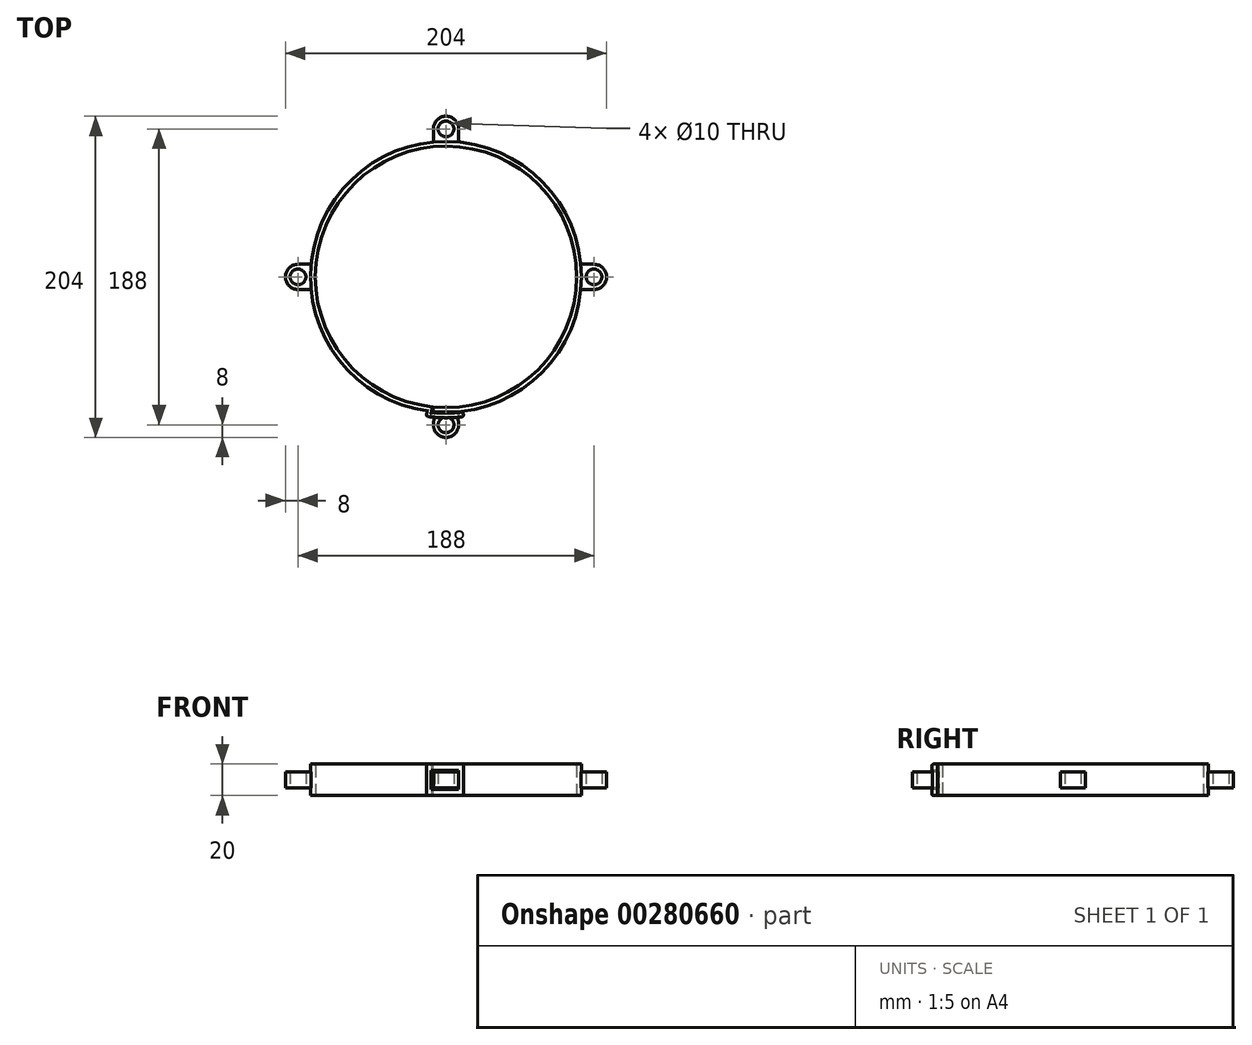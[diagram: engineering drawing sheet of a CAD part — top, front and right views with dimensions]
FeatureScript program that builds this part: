
annotation { "Feature Type Name" : "Feature", "Feature Type Description" : "" }
export const myFeature = defineFeature(function(context is Context, id is Id, definition is map)
    precondition{}
    {
        {
            var Q0;
            Q0=qCreatedBy(makeId("Right.planeOp"),FACE);
            var sketch = newSketch(context, id + "F0", { "sketchPlane" : qUnion([Q0])});
            skLineSegment(sketch, "E0.bottom", {"start": v(83, -10) * mm, "end": v(86, -10) * mm});
            skLineSegment(sketch, "E0.top", {"start": v(83, 10) * mm, "end": v(86, 10) * mm});
            skLineSegment(sketch, "E0.left", {"start": v(83, -10) * mm, "end": v(83, 10) * mm});
            skLineSegment(sketch, "E0.right", {"start": v(86, -10) * mm, "end": v(86, 10) * mm});
            skLineSegment(sketch, "E1", {"start": v(0, 0) * mm, "end": v(0, 60.92) * mm, "construction": true});
            skLineSegment(sketch, "E2", {"start": v(0, 0) * mm, "end": v(83, 0) * mm, "construction": true});
            skSolve(sketch);
        }
        {
            var Q0;
            Q0=makeQuery(id+"F0.imprint","IMPRINT",FACE,{"disambiguationData":[TD([[makeQuery(id+"F0.imprint","IMPRINT",EDGE,{"derivedFrom":sQuery(id+"F0.wireOp",EDGE,"E0.bottom")}),1.0]])]});
            var Q1;
            Q1=sQuery(id+"F0.wireOp",EDGE,"E1");
            revolve(context, id + "F1", {"entities" : qUnion([Q0]), "axis" : qUnion([Q1]), "revolveType" : RevolveType.FULL});
        }
        {
            var Q0;
            Q0=qCreatedBy(makeId("Top.planeOp"),FACE);
            var sketch = newSketch(context, id + "F2", { "sketchPlane" : qUnion([Q0])});
            skLineSegment(sketch, "E3", {"start": v(0, 0) * mm, "end": v(0, 94) * mm, "construction": true});
            skCircle(sketch, "E4", {"center": v(0, 94) * mm, "radius": 8 * mm});
            skCircle(sketch, "E5", {"center": v(0, 94) * mm, "radius": 5 * mm});
            skLineSegment(sketch, "E6", {"start": v(-8, 94) * mm, "end": v(-8, 85.63) * mm});
            skLineSegment(sketch, "E7.MirrorCS", {"start": v(8, 94) * mm, "end": v(8, 85.63) * mm});
            skCircle(sketch, "E8.0", {"center": v(0, 0) * mm, "radius": 86 * mm});
            skCircle(sketch, "E9.0", {"center": v(0, 0) * mm, "radius": 83 * mm});
            skLineSegment(sketch, "E10", {"start": v(0, 0) * mm, "end": v(0, -94) * mm, "construction": true});
            skCircle(sketch, "E11", {"center": v(0, -94) * mm, "radius": 8 * mm});
            skCircle(sketch, "E12", {"center": v(0, -94) * mm, "radius": 5 * mm});
            skLineSegment(sketch, "E13", {"start": v(-7.32, -85.69) * mm, "end": v(-7.97, -93.32) * mm});
            skLineSegment(sketch, "E14.MirrorCS", {"start": v(7.32, -85.69) * mm, "end": v(7.97, -93.32) * mm});
            skCircle(sketch, "E15.0", {"center": v(0, 0) * mm, "radius": 86.5 * mm});
            skCircle(sketch, "E16.0", {"center": v(0, 0) * mm, "radius": 89.5 * mm});
            skLineSegment(sketch, "E17.0", {"start": v(7.86, -86.14) * mm, "end": v(8.12, -89.13) * mm});
            skLineSegment(sketch, "E18.0", {"start": v(10.84, -85.82) * mm, "end": v(11.1, -88.8) * mm});
            skLineSegment(sketch, "E19", {"start": v(-9.14, -86.02) * mm, "end": v(-9.4, -89) * mm});
            skLineSegment(sketch, "E20", {"start": v(-9.14, -86.02) * mm, "end": v(-8.84, -82.53) * mm});
            skLineSegment(sketch, "E21", {"start": v(-8.6, -85.57) * mm, "end": v(-8.34, -82.58) * mm});
            skLineSegment(sketch, "E22", {"start": v(-11.82, -82.15) * mm, "end": v(-12.38, -88.64) * mm});
            skCircle(sketch, "E23.1.0", {"center": v(94, 0) * mm, "radius": 5 * mm});
            skCircle(sketch, "E23.1.1", {"center": v(94, 0) * mm, "radius": 8 * mm});
            skLineSegment(sketch, "E23.1.2", {"start": v(94, 8) * mm, "end": v(85.63, 8) * mm});
            skLineSegment(sketch, "E23.1.3", {"start": v(94, -8) * mm, "end": v(85.63, -8) * mm});
            skLineSegment(sketch, "E23.anchor1", {"start": v(0, 0) * mm, "end": v(-8, 85.63) * mm, "construction": true});
            skLineSegment(sketch, "E23.anchor2", {"start": v(0, 0) * mm, "end": v(85.63, 8) * mm, "construction": true});
            skCircle(sketch, "E24.1.0", {"center": v(-94, 0) * mm, "radius": 8 * mm});
            skLineSegment(sketch, "E24.1.1", {"start": v(-94, -8) * mm, "end": v(-85.63, -8) * mm});
            skLineSegment(sketch, "E24.1.2", {"start": v(-94, 8) * mm, "end": v(-85.63, 8) * mm});
            skCircle(sketch, "E24.1.3", {"center": v(-94, 0) * mm, "radius": 5 * mm});
            skLineSegment(sketch, "E24.anchor2", {"start": v(0, 0) * mm, "end": v(-85.63, -8) * mm, "construction": true});
            skSolve(sketch);
        }
        {
            var Q0;
            {var subQ0=sQuery(id+"F2.wireOp",EDGE,"E8.0");var subQ1=sQuery(id+"F2.wireOp",EDGE,"E4");var subQ2=makeQuery(id+"F2.imprint","INTERSECT",VERTEX,{"derivedFrom":[subQ1,subQ0]});Q0=makeQuery(id+"F2.imprint","IMPRINT",FACE,{"disambiguationData":[TD([[makeQuery(id+"F2.imprint","IMPRINT",EDGE,{"disambiguationData":[TD([[subQ2,-1.0]])],"derivedFrom":subQ1}),-1.0]])]});}
            var Q1;
            {var subQ0=sQuery(id+"F2.wireOp",EDGE,"E15.0");var subQ1=sQuery(id+"F2.wireOp",EDGE,"E4");var subQ2=makeQuery(id+"F2.imprint","INTERSECT",VERTEX,{"disambiguationData":[OD(0.0)],"derivedFrom":[subQ1,subQ0]});Q1=makeQuery(id+"F2.imprint","IMPRINT",FACE,{"disambiguationData":[TD([[makeQuery(id+"F2.imprint","IMPRINT",EDGE,{"disambiguationData":[TD([[subQ2,-1.0]])],"derivedFrom":subQ1}),1.0]])]});}
            var Q2;
            {var subQ0=sQuery(id+"F2.wireOp",EDGE,"E15.0");var subQ1=sQuery(id+"F2.wireOp",EDGE,"E4");var subQ2=makeQuery(id+"F2.imprint","INTERSECT",VERTEX,{"disambiguationData":[OD(0.0)],"derivedFrom":[subQ1,subQ0]});Q2=makeQuery(id+"F2.imprint","IMPRINT",FACE,{"disambiguationData":[TD([[makeQuery(id+"F2.imprint","IMPRINT",EDGE,{"disambiguationData":[TD([[subQ2,-1.0]])],"derivedFrom":subQ1}),-1.0]])]});}
            var Q3;
            {var subQ0=sQuery(id+"F2.wireOp",EDGE,"E16.0");var subQ1=sQuery(id+"F2.wireOp",EDGE,"E4");var subQ2=makeQuery(id+"F2.imprint","INTERSECT",VERTEX,{"disambiguationData":[OD(0.0)],"derivedFrom":[subQ1,subQ0]});Q3=makeQuery(id+"F2.imprint","IMPRINT",FACE,{"disambiguationData":[TD([[makeQuery(id+"F2.imprint","IMPRINT",EDGE,{"disambiguationData":[TD([[subQ2,-1.0]])],"derivedFrom":subQ1}),-1.0]])]});}
            var Q4;
            {var subQ0=sQuery(id+"F2.wireOp",EDGE,"E15.0");var subQ1=sQuery(id+"F2.wireOp",EDGE,"E4");var subQ2=makeQuery(id+"F2.imprint","INTERSECT",VERTEX,{"disambiguationData":[OD(1.0)],"derivedFrom":[subQ1,subQ0]});Q4=makeQuery(id+"F2.imprint","IMPRINT",FACE,{"disambiguationData":[TD([[makeQuery(id+"F2.imprint","IMPRINT",EDGE,{"disambiguationData":[TD([[subQ2,-1.0]])],"derivedFrom":subQ1}),-1.0]])]});}
            var Q5;
            {var subQ0=sQuery(id+"F2.wireOp",EDGE,"E7.MirrorCS");var subQ1=sQuery(id+"F2.wireOp",EDGE,"E4");var subQ2=makeQuery(id+"F2.imprint","INTERSECT",VERTEX,{"derivedFrom":[subQ1,subQ0]});Q5=makeQuery(id+"F2.imprint","IMPRINT",FACE,{"disambiguationData":[TD([[makeQuery(id+"F2.imprint","IMPRINT",EDGE,{"disambiguationData":[TD([[subQ2,1.0]])],"derivedFrom":subQ1}),-1.0]])]});}
            var Q6;
            {var subQ0=sQuery(id+"F2.wireOp",EDGE,"E6");var subQ1=sQuery(id+"F2.wireOp",EDGE,"E4");var subQ2=makeQuery(id+"F2.imprint","INTERSECT",VERTEX,{"derivedFrom":[subQ1,subQ0]});Q6=makeQuery(id+"F2.imprint","IMPRINT",FACE,{"disambiguationData":[TD([[makeQuery(id+"F2.imprint","IMPRINT",EDGE,{"disambiguationData":[TD([[subQ2,-1.0]])],"derivedFrom":subQ1}),-1.0]])]});}
            var Q7;
            {var subQ4=sQuery(id+"F2.wireOp",EDGE,"E4");var subQ7=makeQuery(id+"F2.imprint","INTERSECT",VERTEX,{"derivedFrom":[subQ4,sQuery(id+"F2.wireOp",EDGE,"E6")]});Q7=makeQuery(id+"F2.imprint","IMPRINT",FACE,{"disambiguationData":[TD([[makeQuery(id+"F2.imprint","IMPRINT",EDGE,{"disambiguationData":[TD([[subQ7,1.0]])],"derivedFrom":subQ4}),1.0]])]});}
            var Q8;
            {var subQ1=sQuery(id+"F2.wireOp",EDGE,"E4");var subQ4=sQuery(id+"F2.wireOp",EDGE,"E16.0");var subQ9=makeQuery(id+"F2.imprint","INTERSECT",VERTEX,{"disambiguationData":[OD(0.0)],"derivedFrom":[subQ1,subQ4]});Q8=makeQuery(id+"F2.imprint","IMPRINT",FACE,{"disambiguationData":[TD([[makeQuery(id+"F2.imprint","IMPRINT",EDGE,{"disambiguationData":[TD([[subQ9,-1.0]])],"derivedFrom":subQ1}),1.0]])]});}
            extrude(context, id + "F3", {"entities" : qUnion([Q0, Q1, Q2, Q3, Q4, Q5, Q6, Q7, Q8]), "operationType" : NewBodyOperationType.ADD, "endBound" : BoundingType.SYMMETRIC, "depth" : 10 * mm});
        }
        {
            var Q0;
            {var subQ0=sQuery(id+"F2.wireOp",EDGE,"E21");Q0=makeQuery(id+"F2.imprint","IMPRINT",FACE,{"disambiguationData":[TD([[makeQuery(id+"F2.imprint","IMPRINT",EDGE,{"derivedFrom":subQ0}),1.0]])]});}
            extrude(context, id + "F4", {"entities" : qUnion([Q0]), "operationType" : NewBodyOperationType.REMOVE, "endBound" : BoundingType.THROUGH_ALL, "oppositeDirection" : true, "depth" : 20 * mm});
        }
        {
            var Q0;
            {var subQ0=sQuery(id+"F2.wireOp",EDGE,"E21");Q0=makeQuery(id+"F2.imprint","IMPRINT",FACE,{"disambiguationData":[TD([[makeQuery(id+"F2.imprint","IMPRINT",EDGE,{"derivedFrom":subQ0}),1.0]])]});}
            extrude(context, id + "F5", {"entities" : qUnion([Q0]), "operationType" : NewBodyOperationType.REMOVE, "endBound" : BoundingType.THROUGH_ALL, "depth" : 25 * mm});
        }
        {
            var Q0;
            {var subQ0=sQuery(id+"F2.wireOp",EDGE,"E22");var subQ1=sQuery(id+"F2.wireOp",EDGE,"E8.0");var subQ2=makeQuery(id+"F2.imprint","INTERSECT",VERTEX,{"derivedFrom":[subQ1,subQ0]});Q0=makeQuery(id+"F2.imprint","IMPRINT",FACE,{"disambiguationData":[TD([[makeQuery(id+"F2.imprint","IMPRINT",EDGE,{"disambiguationData":[TD([[subQ2,-1.0]])],"derivedFrom":subQ1}),-1.0]])]});}
            var Q1;
            {var subQ0=sQuery(id+"F2.wireOp",EDGE,"E19");Q1=makeQuery(id+"F2.imprint","IMPRINT",FACE,{"disambiguationData":[TD([[makeQuery(id+"F2.imprint","IMPRINT",EDGE,{"derivedFrom":subQ0}),-1.0]])]});}
            var Q2;
            {var subQ5=sQuery(id+"F2.wireOp",EDGE,"E19");Q2=makeQuery(id+"F2.imprint","IMPRINT",FACE,{"disambiguationData":[TD([[makeQuery(id+"F2.imprint","IMPRINT",EDGE,{"derivedFrom":subQ5}),1.0]])]});}
            var Q3;
            {var subQ0=sQuery(id+"F2.wireOp",EDGE,"E15.0");var subQ1=sQuery(id+"F2.wireOp",EDGE,"E11");var subQ2=makeQuery(id+"F2.imprint","INTERSECT",VERTEX,{"disambiguationData":[OD(1.0)],"derivedFrom":[subQ1,subQ0]});Q3=makeQuery(id+"F2.imprint","IMPRINT",FACE,{"disambiguationData":[TD([[makeQuery(id+"F2.imprint","IMPRINT",EDGE,{"disambiguationData":[TD([[subQ2,-1.0]])],"derivedFrom":subQ1}),-1.0]])]});}
            var Q4;
            {var subQ1=sQuery(id+"F2.wireOp",EDGE,"E11");var subQ4=sQuery(id+"F2.wireOp",EDGE,"E16.0");var subQ9=makeQuery(id+"F2.imprint","INTERSECT",VERTEX,{"disambiguationData":[OD(0.0)],"derivedFrom":[subQ1,subQ4]});Q4=makeQuery(id+"F2.imprint","IMPRINT",FACE,{"disambiguationData":[TD([[makeQuery(id+"F2.imprint","IMPRINT",EDGE,{"disambiguationData":[TD([[subQ9,-1.0]])],"derivedFrom":subQ1}),1.0]])]});}
            var Q5;
            {var subQ0=sQuery(id+"F2.wireOp",EDGE,"E16.0");var subQ1=sQuery(id+"F2.wireOp",EDGE,"E12");var subQ2=makeQuery(id+"F2.imprint","INTERSECT",VERTEX,{"disambiguationData":[OD(0.0)],"derivedFrom":[subQ1,subQ0]});Q5=makeQuery(id+"F2.imprint","IMPRINT",FACE,{"disambiguationData":[TD([[makeQuery(id+"F2.imprint","IMPRINT",EDGE,{"disambiguationData":[TD([[subQ2,1.0]])],"derivedFrom":subQ1}),1.0]])]});}
            var Q6;
            {var subQ0=sQuery(id+"F2.wireOp",EDGE,"E16.0");var subQ1=sQuery(id+"F2.wireOp",EDGE,"E11");var subQ2=makeQuery(id+"F2.imprint","INTERSECT",VERTEX,{"disambiguationData":[OD(0.0)],"derivedFrom":[subQ1,subQ0]});Q6=makeQuery(id+"F2.imprint","IMPRINT",FACE,{"disambiguationData":[TD([[makeQuery(id+"F2.imprint","IMPRINT",EDGE,{"disambiguationData":[TD([[subQ2,-1.0]])],"derivedFrom":subQ1}),-1.0]])]});}
            var Q7;
            {var subQ5=sQuery(id+"F2.wireOp",EDGE,"E17.0");Q7=makeQuery(id+"F2.imprint","IMPRINT",FACE,{"disambiguationData":[TD([[makeQuery(id+"F2.imprint","IMPRINT",EDGE,{"derivedFrom":subQ5}),-1.0]])]});}
            var Q8;
            {var subQ0=sQuery(id+"F2.wireOp",EDGE,"E17.0");Q8=makeQuery(id+"F2.imprint","IMPRINT",FACE,{"disambiguationData":[TD([[makeQuery(id+"F2.imprint","IMPRINT",EDGE,{"derivedFrom":subQ0}),1.0]])]});}
            extrude(context, id + "F6", {"entities" : qUnion([Q0, Q1, Q2, Q3, Q4, Q5, Q6, Q7, Q8]), "operationType" : NewBodyOperationType.ADD, "endBound" : BoundingType.SYMMETRIC, "depth" : 20 * mm});
        }
        {
            var Q0;
            {var subQ5=sQuery(id+"F2.wireOp",EDGE,"E19");Q0=makeQuery(id+"F2.imprint","IMPRINT",FACE,{"disambiguationData":[TD([[makeQuery(id+"F2.imprint","IMPRINT",EDGE,{"derivedFrom":subQ5}),1.0]])]});}
            var Q1;
            {var subQ0=sQuery(id+"F2.wireOp",EDGE,"E15.0");var subQ1=sQuery(id+"F2.wireOp",EDGE,"E11");var subQ2=makeQuery(id+"F2.imprint","INTERSECT",VERTEX,{"disambiguationData":[OD(1.0)],"derivedFrom":[subQ1,subQ0]});Q1=makeQuery(id+"F2.imprint","IMPRINT",FACE,{"disambiguationData":[TD([[makeQuery(id+"F2.imprint","IMPRINT",EDGE,{"disambiguationData":[TD([[subQ2,-1.0]])],"derivedFrom":subQ1}),-1.0]])]});}
            var Q2;
            {var subQ1=sQuery(id+"F2.wireOp",EDGE,"E11");var subQ4=sQuery(id+"F2.wireOp",EDGE,"E16.0");var subQ9=makeQuery(id+"F2.imprint","INTERSECT",VERTEX,{"disambiguationData":[OD(0.0)],"derivedFrom":[subQ1,subQ4]});Q2=makeQuery(id+"F2.imprint","IMPRINT",FACE,{"disambiguationData":[TD([[makeQuery(id+"F2.imprint","IMPRINT",EDGE,{"disambiguationData":[TD([[subQ9,-1.0]])],"derivedFrom":subQ1}),1.0]])]});}
            var Q3;
            {var subQ0=sQuery(id+"F2.wireOp",EDGE,"E16.0");var subQ1=sQuery(id+"F2.wireOp",EDGE,"E12");var subQ2=makeQuery(id+"F2.imprint","INTERSECT",VERTEX,{"disambiguationData":[OD(0.0)],"derivedFrom":[subQ1,subQ0]});Q3=makeQuery(id+"F2.imprint","IMPRINT",FACE,{"disambiguationData":[TD([[makeQuery(id+"F2.imprint","IMPRINT",EDGE,{"disambiguationData":[TD([[subQ2,1.0]])],"derivedFrom":subQ1}),1.0]])]});}
            var Q4;
            {var subQ0=sQuery(id+"F2.wireOp",EDGE,"E16.0");var subQ1=sQuery(id+"F2.wireOp",EDGE,"E11");var subQ2=makeQuery(id+"F2.imprint","INTERSECT",VERTEX,{"disambiguationData":[OD(0.0)],"derivedFrom":[subQ1,subQ0]});Q4=makeQuery(id+"F2.imprint","IMPRINT",FACE,{"disambiguationData":[TD([[makeQuery(id+"F2.imprint","IMPRINT",EDGE,{"disambiguationData":[TD([[subQ2,-1.0]])],"derivedFrom":subQ1}),-1.0]])]});}
            var Q5;
            {var subQ5=sQuery(id+"F2.wireOp",EDGE,"E17.0");Q5=makeQuery(id+"F2.imprint","IMPRINT",FACE,{"disambiguationData":[TD([[makeQuery(id+"F2.imprint","IMPRINT",EDGE,{"derivedFrom":subQ5}),-1.0]])]});}
            extrude(context, id + "F7", {"entities" : qUnion([Q0, Q1, Q2, Q3, Q4, Q5]), "operationType" : NewBodyOperationType.REMOVE, "endBound" : BoundingType.SYMMETRIC, "oppositeDirection" : true, "depth" : 12 * mm});
        }
        {
            var Q0;
            {var subQ0=sQuery(id+"F2.wireOp",EDGE,"E13");var subQ1=sQuery(id+"F2.wireOp",EDGE,"E8.0");var subQ2=makeQuery(id+"F2.imprint","INTERSECT",VERTEX,{"derivedFrom":[subQ1,subQ0]});Q0=makeQuery(id+"F2.imprint","IMPRINT",FACE,{"disambiguationData":[TD([[makeQuery(id+"F2.imprint","IMPRINT",EDGE,{"disambiguationData":[TD([[subQ2,-1.0]])],"derivedFrom":subQ1}),-1.0]])]});}
            var Q1;
            {var subQ0=sQuery(id+"F2.wireOp",EDGE,"E11");var subQ1=makeQuery(id+"F2.imprint","INTERSECT",VERTEX,{"derivedFrom":[sQuery(id+"F2.wireOp",EDGE,"E8.0"),subQ0]});Q1=makeQuery(id+"F2.imprint","IMPRINT",FACE,{"disambiguationData":[TD([[makeQuery(id+"F2.imprint","IMPRINT",EDGE,{"disambiguationData":[TD([[subQ1,1.0]])],"derivedFrom":subQ0}),1.0]])]});}
            var Q2;
            {var subQ0=sQuery(id+"F2.wireOp",EDGE,"E14.MirrorCS");var subQ1=sQuery(id+"F2.wireOp",EDGE,"E8.0");var subQ2=makeQuery(id+"F2.imprint","INTERSECT",VERTEX,{"derivedFrom":[subQ1,subQ0]});Q2=makeQuery(id+"F2.imprint","IMPRINT",FACE,{"disambiguationData":[TD([[makeQuery(id+"F2.imprint","IMPRINT",EDGE,{"disambiguationData":[TD([[subQ2,1.0]])],"derivedFrom":subQ1}),-1.0]])]});}
            var Q3;
            {var subQ0=sQuery(id+"F2.wireOp",EDGE,"E16.0");var subQ1=sQuery(id+"F2.wireOp",EDGE,"E11");var subQ2=makeQuery(id+"F2.imprint","INTERSECT",VERTEX,{"disambiguationData":[OD(0.0)],"derivedFrom":[subQ1,subQ0]});Q3=makeQuery(id+"F2.imprint","IMPRINT",FACE,{"disambiguationData":[TD([[makeQuery(id+"F2.imprint","IMPRINT",EDGE,{"disambiguationData":[TD([[subQ2,-1.0]])],"derivedFrom":subQ1}),-1.0]])]});}
            var Q4;
            {var subQ1=sQuery(id+"F2.wireOp",EDGE,"E11");var subQ4=sQuery(id+"F2.wireOp",EDGE,"E16.0");var subQ9=makeQuery(id+"F2.imprint","INTERSECT",VERTEX,{"disambiguationData":[OD(0.0)],"derivedFrom":[subQ1,subQ4]});Q4=makeQuery(id+"F2.imprint","IMPRINT",FACE,{"disambiguationData":[TD([[makeQuery(id+"F2.imprint","IMPRINT",EDGE,{"disambiguationData":[TD([[subQ9,-1.0]])],"derivedFrom":subQ1}),1.0]])]});}
            var Q5;
            {var subQ0=sQuery(id+"F2.wireOp",EDGE,"E15.0");var subQ1=sQuery(id+"F2.wireOp",EDGE,"E11");var subQ2=makeQuery(id+"F2.imprint","INTERSECT",VERTEX,{"disambiguationData":[OD(1.0)],"derivedFrom":[subQ1,subQ0]});Q5=makeQuery(id+"F2.imprint","IMPRINT",FACE,{"disambiguationData":[TD([[makeQuery(id+"F2.imprint","IMPRINT",EDGE,{"disambiguationData":[TD([[subQ2,-1.0]])],"derivedFrom":subQ1}),-1.0]])]});}
            var Q6;
            {var subQ0=sQuery(id+"F2.wireOp",EDGE,"E13");var subQ1=sQuery(id+"F2.wireOp",EDGE,"E11");var subQ2=makeQuery(id+"F2.imprint","INTERSECT",VERTEX,{"derivedFrom":[subQ1,subQ0]});Q6=makeQuery(id+"F2.imprint","IMPRINT",FACE,{"disambiguationData":[TD([[makeQuery(id+"F2.imprint","IMPRINT",EDGE,{"disambiguationData":[TD([[subQ2,1.0]])],"derivedFrom":subQ1}),-1.0]])]});}
            var Q7;
            {var subQ0=sQuery(id+"F2.wireOp",EDGE,"E14.MirrorCS");var subQ1=sQuery(id+"F2.wireOp",EDGE,"E11");var subQ2=makeQuery(id+"F2.imprint","INTERSECT",VERTEX,{"derivedFrom":[subQ1,subQ0]});Q7=makeQuery(id+"F2.imprint","IMPRINT",FACE,{"disambiguationData":[TD([[makeQuery(id+"F2.imprint","IMPRINT",EDGE,{"disambiguationData":[TD([[subQ2,-1.0]])],"derivedFrom":subQ1}),-1.0]])]});}
            var Q8;
            {var subQ4=sQuery(id+"F2.wireOp",EDGE,"E11");var subQ6=makeQuery(id+"F2.imprint","INTERSECT",VERTEX,{"derivedFrom":[subQ4,sQuery(id+"F2.wireOp",EDGE,"E14.MirrorCS")]});Q8=makeQuery(id+"F2.imprint","IMPRINT",FACE,{"disambiguationData":[TD([[makeQuery(id+"F2.imprint","IMPRINT",EDGE,{"disambiguationData":[TD([[subQ6,-1.0]])],"derivedFrom":subQ4}),1.0]])]});}
            extrude(context, id + "F8", {"entities" : qUnion([Q0, Q1, Q2, Q3, Q4, Q5, Q6, Q7, Q8]), "operationType" : NewBodyOperationType.ADD, "endBound" : BoundingType.SYMMETRIC, "depth" : 10 * mm});
        }
        {
            var Q0;
            Q0=makeQuery(id+"F6.opExtrude","CAP_EDGE",EDGE,{"disambiguationData":[OSD([sQuery(id+"F2.wireOp",EDGE,"E16.0")])],"isStart":false});
            var Q1;
            Q1=makeQuery(id+"F6.opExtrude","SWEPT_EDGE",EDGE,{"disambiguationData":[OSD([sQuery(id+"F2.wireOp",EDGE,"E16.0"),sQuery(id+"F2.wireOp",EDGE,"E18.0")])]});
            var Q2;
            Q2=makeQuery(id+"F6.opExtrude","CAP_EDGE",EDGE,{"disambiguationData":[OSD([sQuery(id+"F2.wireOp",EDGE,"E18.0")])],"isStart":false});
            var Q3;
            Q3=makeQuery(id+"F6.opExtrude","CAP_EDGE",EDGE,{"disambiguationData":[OSD([sQuery(id+"F2.wireOp",EDGE,"E18.0")])],"isStart":true});
            var Q4;
            Q4=makeQuery(id+"F6.opExtrude","CAP_EDGE",EDGE,{"disambiguationData":[OSD([sQuery(id+"F2.wireOp",EDGE,"E16.0")])],"isStart":true});
            var Q5;
            Q5=makeQuery(id+"F6.opExtrude","SWEPT_EDGE",EDGE,{"disambiguationData":[OSD([sQuery(id+"F2.wireOp",EDGE,"E16.0"),sQuery(id+"F2.wireOp",EDGE,"E22")])]});
            var Q6;
            Q6=makeQuery(id+"F6.opExtrude","SWEPT_EDGE",EDGE,{"disambiguationData":[OSD([sQuery(id+"F2.wireOp",EDGE,"E8.0"),sQuery(id+"F2.wireOp",EDGE,"E22")])]});
            var Q7;
            Q7=makeQuery(id+"F6.opExtrude","CAP_EDGE",EDGE,{"disambiguationData":[OSD([sQuery(id+"F2.wireOp",EDGE,"E22")])],"isStart":false});
            var Q8;
            Q8=makeQuery(id+"F6.opExtrude","CAP_EDGE",EDGE,{"disambiguationData":[OSD([sQuery(id+"F2.wireOp",EDGE,"E22")])],"isStart":true});
            var Q9;
            {var subQ0=sQuery(id+"F2.wireOp",EDGE,"E20");Q9=makeQuery(id+"F6.boolean.opBoolean","MERGE",EDGE,{"derivedFrom":[makeQuery(id+"F5.boolean.opBoolean","INTERSECT",EDGE,{"derivedFrom":[makeQuery(id+"F1.opRevolve","SWEPT_FACE",FACE,{"disambiguationData":[OSD([sQuery(id+"F0.wireOp",EDGE,"E0.top")])]}),makeQuery(id+"F5.opExtrude","SWEPT_FACE",FACE,{"disambiguationData":[OSD([subQ0])]})]}),makeQuery(id+"F6.opExtrude","CAP_EDGE",EDGE,{"disambiguationData":[OSD([subQ0])],"isStart":false})]});}
            var Q10;
            Q10=makeQuery(id+"F5.boolean.opBoolean","INTERSECT",EDGE,{"derivedFrom":[makeQuery(id+"F1.opRevolve","SWEPT_FACE",FACE,{"disambiguationData":[OSD([sQuery(id+"F0.wireOp",EDGE,"E0.top")])]}),makeQuery(id+"F5.opExtrude","SWEPT_FACE",FACE,{"disambiguationData":[OSD([sQuery(id+"F2.wireOp",EDGE,"E21")])]})]});
            var Q11;
            Q11=makeQuery(id+"F1.opRevolve","SWEPT_EDGE",EDGE,{"disambiguationData":[OSD([sQuery(id+"F0.wireOp",EDGE,"E0.top"),sQuery(id+"F0.wireOp",EDGE,"E0.left")])]});
            var Q12;
            Q12=makeQuery(id+"F1.opRevolve","SWEPT_EDGE",EDGE,{"disambiguationData":[OSD([sQuery(id+"F0.wireOp",EDGE,"E0.bottom"),sQuery(id+"F0.wireOp",EDGE,"E0.left")])]});
            var Q13;
            Q13=makeQuery(id+"F4.boolean.opBoolean","INTERSECT",EDGE,{"derivedFrom":[makeQuery(id+"F1.opRevolve","SWEPT_FACE",FACE,{"disambiguationData":[OSD([sQuery(id+"F0.wireOp",EDGE,"E0.bottom")])]}),makeQuery(id+"F4.opExtrude","SWEPT_FACE",FACE,{"disambiguationData":[OSD([sQuery(id+"F2.wireOp",EDGE,"E21")])]})]});
            var Q14;
            {var subQ0=sQuery(id+"F2.wireOp",EDGE,"E20");Q14=makeQuery(id+"F6.boolean.opBoolean","MERGE",EDGE,{"derivedFrom":[makeQuery(id+"F4.boolean.opBoolean","INTERSECT",EDGE,{"derivedFrom":[makeQuery(id+"F1.opRevolve","SWEPT_FACE",FACE,{"disambiguationData":[OSD([sQuery(id+"F0.wireOp",EDGE,"E0.bottom")])]}),makeQuery(id+"F4.opExtrude","SWEPT_FACE",FACE,{"disambiguationData":[OSD([subQ0])]})]}),makeQuery(id+"F6.opExtrude","CAP_EDGE",EDGE,{"disambiguationData":[OSD([subQ0])],"isStart":true})]});}
            var Q15;
            {var subQ0=sQuery(id+"F2.wireOp",EDGE,"E21");var subQ1=sQuery(id+"F2.wireOp",EDGE,"E9.0");Q15=makeQuery(id+"F5.boolean.opBoolean","MERGE",EDGE,{"derivedFrom":[makeQuery(id+"F4.boolean.opBoolean","COPY",EDGE,{"derivedFrom":makeQuery(id+"F4.opExtrude","SWEPT_EDGE",EDGE,{"disambiguationData":[OSD([subQ1,subQ0])]})}),makeQuery(id+"F5.opExtrude","SWEPT_EDGE",EDGE,{"disambiguationData":[OSD([subQ1,subQ0])]})]});}
            var Q16;
            {var subQ0=sQuery(id+"F2.wireOp",EDGE,"E20");var subQ1=sQuery(id+"F2.wireOp",EDGE,"E9.0");Q16=makeQuery(id+"F5.boolean.opBoolean","MERGE",EDGE,{"derivedFrom":[makeQuery(id+"F4.boolean.opBoolean","COPY",EDGE,{"derivedFrom":makeQuery(id+"F4.opExtrude","SWEPT_EDGE",EDGE,{"disambiguationData":[OSD([subQ1,subQ0])]})}),makeQuery(id+"F5.opExtrude","SWEPT_EDGE",EDGE,{"disambiguationData":[OSD([subQ1,subQ0])]})]});}
            var Q17;
            Q17=makeQuery(id+"F3.opExtrude","CAP_EDGE",EDGE,{"disambiguationData":[OSD([sQuery(id+"F2.wireOp",EDGE,"E8.0")])],"isStart":false});
            var Q18;
            Q18=makeQuery(id+"F3.opExtrude","SWEPT_EDGE",EDGE,{"disambiguationData":[OSD([sQuery(id+"F2.wireOp",EDGE,"E7.MirrorCS"),sQuery(id+"F2.wireOp",EDGE,"E8.0")])]});
            var Q19;
            Q19=makeQuery(id+"F3.opExtrude","SWEPT_EDGE",EDGE,{"disambiguationData":[OSD([sQuery(id+"F2.wireOp",EDGE,"E6"),sQuery(id+"F2.wireOp",EDGE,"E8.0")])]});
            var Q20;
            Q20=makeQuery(id+"F3.opExtrude","CAP_EDGE",EDGE,{"disambiguationData":[OSD([sQuery(id+"F2.wireOp",EDGE,"E8.0")])],"isStart":true});
            var Q21;
            Q21=makeQuery(id+"F6.opExtrude","CAP_EDGE",EDGE,{"disambiguationData":[OSD([sQuery(id+"F2.wireOp",EDGE,"E15.0")])],"isStart":false});
            var Q22;
            Q22=makeQuery(id+"F6.opExtrude","CAP_EDGE",EDGE,{"disambiguationData":[OSD([sQuery(id+"F2.wireOp",EDGE,"E15.0")])],"isStart":true});
            var Q23;
            Q23=makeQuery(id+"F6.opExtrude","SWEPT_EDGE",EDGE,{"disambiguationData":[OSD([sQuery(id+"F2.wireOp",EDGE,"E15.0"),sQuery(id+"F2.wireOp",EDGE,"E18.0")])]});
            fillet(context, id + "F9", {"entities" : qUnion([Q0, Q1, Q2, Q3, Q4, Q5, Q6, Q7, Q8, Q9, Q10, Q11, Q12, Q13, Q14, Q15, Q16, Q17, Q18, Q19, Q20, Q21, Q22, Q23]), "radius" : 1 * mm, "tangentPropagation" : true, "allowEdgeOverflow" : false});
        }
        {
            var Q0;
            {var subQ0=sQuery(id+"F2.wireOp",EDGE,"E24.1.2");var subQ1=sQuery(id+"F2.wireOp",EDGE,"E8.0");var subQ2=makeQuery(id+"F2.imprint","INTERSECT",VERTEX,{"derivedFrom":[subQ1,subQ0]});Q0=makeQuery(id+"F2.imprint","IMPRINT",FACE,{"disambiguationData":[TD([[makeQuery(id+"F2.imprint","IMPRINT",EDGE,{"disambiguationData":[TD([[subQ2,-1.0]])],"derivedFrom":subQ1}),-1.0]])]});}
            var Q1;
            {var subQ0=sQuery(id+"F2.wireOp",EDGE,"E24.1.0");var subQ1=sQuery(id+"F2.wireOp",EDGE,"E15.0");var subQ2=makeQuery(id+"F2.imprint","INTERSECT",VERTEX,{"disambiguationData":[OD(0.0)],"derivedFrom":[subQ1,subQ0]});Q1=makeQuery(id+"F2.imprint","IMPRINT",FACE,{"disambiguationData":[TD([[makeQuery(id+"F2.imprint","IMPRINT",EDGE,{"disambiguationData":[TD([[subQ2,-1.0]])],"derivedFrom":subQ1}),1.0]])]});}
            var Q2;
            {var subQ0=sQuery(id+"F2.wireOp",EDGE,"E24.1.1");var subQ1=sQuery(id+"F2.wireOp",EDGE,"E8.0");var subQ2=makeQuery(id+"F2.imprint","INTERSECT",VERTEX,{"derivedFrom":[subQ1,subQ0]});Q2=makeQuery(id+"F2.imprint","IMPRINT",FACE,{"disambiguationData":[TD([[makeQuery(id+"F2.imprint","IMPRINT",EDGE,{"disambiguationData":[TD([[subQ2,1.0]])],"derivedFrom":subQ1}),-1.0]])]});}
            var Q3;
            {var subQ0=sQuery(id+"F2.wireOp",EDGE,"E24.1.0");var subQ1=sQuery(id+"F2.wireOp",EDGE,"E15.0");var subQ2=makeQuery(id+"F2.imprint","INTERSECT",VERTEX,{"disambiguationData":[OD(1.0)],"derivedFrom":[subQ1,subQ0]});Q3=makeQuery(id+"F2.imprint","IMPRINT",FACE,{"disambiguationData":[TD([[makeQuery(id+"F2.imprint","IMPRINT",EDGE,{"disambiguationData":[TD([[subQ2,-1.0]])],"derivedFrom":subQ1}),-1.0]])]});}
            var Q4;
            {var subQ0=sQuery(id+"F2.wireOp",EDGE,"E24.1.0");var subQ1=sQuery(id+"F2.wireOp",EDGE,"E15.0");var subQ9=makeQuery(id+"F2.imprint","INTERSECT",VERTEX,{"disambiguationData":[OD(0.0)],"derivedFrom":[subQ1,subQ0]});Q4=makeQuery(id+"F2.imprint","IMPRINT",FACE,{"disambiguationData":[TD([[makeQuery(id+"F2.imprint","IMPRINT",EDGE,{"disambiguationData":[TD([[subQ9,-1.0]])],"derivedFrom":subQ1}),-1.0]])]});}
            var Q5;
            {var subQ0=sQuery(id+"F2.wireOp",EDGE,"E24.1.2");var subQ1=sQuery(id+"F2.wireOp",EDGE,"E15.0");var subQ2=makeQuery(id+"F2.imprint","INTERSECT",VERTEX,{"derivedFrom":[subQ1,subQ0]});Q5=makeQuery(id+"F2.imprint","IMPRINT",FACE,{"disambiguationData":[TD([[makeQuery(id+"F2.imprint","IMPRINT",EDGE,{"disambiguationData":[TD([[subQ2,-1.0]])],"derivedFrom":subQ1}),-1.0]])]});}
            var Q6;
            {var subQ0=sQuery(id+"F2.wireOp",EDGE,"E24.1.2");var subQ1=sQuery(id+"F2.wireOp",EDGE,"E16.0");var subQ2=makeQuery(id+"F2.imprint","INTERSECT",VERTEX,{"derivedFrom":[subQ1,subQ0]});Q6=makeQuery(id+"F2.imprint","IMPRINT",FACE,{"disambiguationData":[TD([[makeQuery(id+"F2.imprint","IMPRINT",EDGE,{"disambiguationData":[TD([[subQ2,-1.0]])],"derivedFrom":subQ1}),-1.0]])]});}
            var Q7;
            {var subQ0=sQuery(id+"F2.wireOp",EDGE,"E24.1.0");var subQ2=sQuery(id+"F2.wireOp",EDGE,"E16.0");var subQ7=makeQuery(id+"F2.imprint","INTERSECT",VERTEX,{"disambiguationData":[OD(0.0)],"derivedFrom":[subQ2,subQ0]});Q7=makeQuery(id+"F2.imprint","IMPRINT",FACE,{"disambiguationData":[TD([[makeQuery(id+"F2.imprint","IMPRINT",EDGE,{"disambiguationData":[TD([[subQ7,-1.0]])],"derivedFrom":subQ2}),-1.0]])]});}
            var Q8;
            {var subQ0=sQuery(id+"F2.wireOp",EDGE,"E24.1.1");var subQ1=sQuery(id+"F2.wireOp",EDGE,"E16.0");var subQ2=makeQuery(id+"F2.imprint","INTERSECT",VERTEX,{"derivedFrom":[subQ1,subQ0]});Q8=makeQuery(id+"F2.imprint","IMPRINT",FACE,{"disambiguationData":[TD([[makeQuery(id+"F2.imprint","IMPRINT",EDGE,{"disambiguationData":[TD([[subQ2,1.0]])],"derivedFrom":subQ1}),-1.0]])]});}
            var Q9;
            {var subQ0=sQuery(id+"F2.wireOp",EDGE,"E23.1.2");var subQ1=sQuery(id+"F2.wireOp",EDGE,"E8.0");var subQ2=makeQuery(id+"F2.imprint","INTERSECT",VERTEX,{"derivedFrom":[subQ1,subQ0]});Q9=makeQuery(id+"F2.imprint","IMPRINT",FACE,{"disambiguationData":[TD([[makeQuery(id+"F2.imprint","IMPRINT",EDGE,{"disambiguationData":[TD([[subQ2,1.0]])],"derivedFrom":subQ1}),-1.0]])]});}
            var Q10;
            {var subQ0=sQuery(id+"F2.wireOp",EDGE,"E23.1.1");var subQ1=sQuery(id+"F2.wireOp",EDGE,"E15.0");var subQ2=makeQuery(id+"F2.imprint","INTERSECT",VERTEX,{"disambiguationData":[OD(0.0)],"derivedFrom":[subQ1,subQ0]});Q10=makeQuery(id+"F2.imprint","IMPRINT",FACE,{"disambiguationData":[TD([[makeQuery(id+"F2.imprint","IMPRINT",EDGE,{"disambiguationData":[TD([[subQ2,1.0]])],"derivedFrom":subQ1}),1.0]])]});}
            var Q11;
            {var subQ0=sQuery(id+"F2.wireOp",EDGE,"E23.1.3");var subQ1=sQuery(id+"F2.wireOp",EDGE,"E8.0");var subQ2=makeQuery(id+"F2.imprint","INTERSECT",VERTEX,{"derivedFrom":[subQ1,subQ0]});Q11=makeQuery(id+"F2.imprint","IMPRINT",FACE,{"disambiguationData":[TD([[makeQuery(id+"F2.imprint","IMPRINT",EDGE,{"disambiguationData":[TD([[subQ2,-1.0]])],"derivedFrom":subQ1}),-1.0]])]});}
            var Q12;
            {var subQ0=sQuery(id+"F2.wireOp",EDGE,"E23.1.3");var subQ1=sQuery(id+"F2.wireOp",EDGE,"E15.0");var subQ2=makeQuery(id+"F2.imprint","INTERSECT",VERTEX,{"derivedFrom":[subQ1,subQ0]});Q12=makeQuery(id+"F2.imprint","IMPRINT",FACE,{"disambiguationData":[TD([[makeQuery(id+"F2.imprint","IMPRINT",EDGE,{"disambiguationData":[TD([[subQ2,-1.0]])],"derivedFrom":subQ1}),-1.0]])]});}
            var Q13;
            {var subQ0=sQuery(id+"F2.wireOp",EDGE,"E23.1.3");var subQ1=sQuery(id+"F2.wireOp",EDGE,"E16.0");var subQ2=makeQuery(id+"F2.imprint","INTERSECT",VERTEX,{"derivedFrom":[subQ1,subQ0]});Q13=makeQuery(id+"F2.imprint","IMPRINT",FACE,{"disambiguationData":[TD([[makeQuery(id+"F2.imprint","IMPRINT",EDGE,{"disambiguationData":[TD([[subQ2,-1.0]])],"derivedFrom":subQ1}),-1.0]])]});}
            var Q14;
            {var subQ4=sQuery(id+"F2.wireOp",EDGE,"E23.1.1");var subQ7=sQuery(id+"F2.wireOp",EDGE,"E15.0");var subQ9=makeQuery(id+"F2.imprint","INTERSECT",VERTEX,{"disambiguationData":[OD(0.0)],"derivedFrom":[subQ7,subQ4]});Q14=makeQuery(id+"F2.imprint","IMPRINT",FACE,{"disambiguationData":[TD([[makeQuery(id+"F2.imprint","IMPRINT",EDGE,{"disambiguationData":[TD([[subQ9,1.0]])],"derivedFrom":subQ7}),-1.0]])]});}
            var Q15;
            {var subQ0=sQuery(id+"F2.wireOp",EDGE,"E23.1.1");var subQ4=sQuery(id+"F2.wireOp",EDGE,"E16.0");var subQ8=makeQuery(id+"F2.imprint","INTERSECT",VERTEX,{"disambiguationData":[OD(0.0)],"derivedFrom":[subQ4,subQ0]});Q15=makeQuery(id+"F2.imprint","IMPRINT",FACE,{"disambiguationData":[TD([[makeQuery(id+"F2.imprint","IMPRINT",EDGE,{"disambiguationData":[TD([[subQ8,1.0]])],"derivedFrom":subQ4}),-1.0]])]});}
            var Q16;
            {var subQ0=sQuery(id+"F2.wireOp",EDGE,"E23.1.2");var subQ1=sQuery(id+"F2.wireOp",EDGE,"E16.0");var subQ2=makeQuery(id+"F2.imprint","INTERSECT",VERTEX,{"derivedFrom":[subQ1,subQ0]});Q16=makeQuery(id+"F2.imprint","IMPRINT",FACE,{"disambiguationData":[TD([[makeQuery(id+"F2.imprint","IMPRINT",EDGE,{"disambiguationData":[TD([[subQ2,1.0]])],"derivedFrom":subQ1}),-1.0]])]});}
            var Q17;
            {var subQ0=sQuery(id+"F2.wireOp",EDGE,"E23.1.2");var subQ1=sQuery(id+"F2.wireOp",EDGE,"E15.0");var subQ2=makeQuery(id+"F2.imprint","INTERSECT",VERTEX,{"derivedFrom":[subQ1,subQ0]});Q17=makeQuery(id+"F2.imprint","IMPRINT",FACE,{"disambiguationData":[TD([[makeQuery(id+"F2.imprint","IMPRINT",EDGE,{"disambiguationData":[TD([[subQ2,1.0]])],"derivedFrom":subQ1}),-1.0]])]});}
            extrude(context, id + "F10", {"entities" : qUnion([Q0, Q1, Q2, Q3, Q4, Q5, Q6, Q7, Q8, Q9, Q10, Q11, Q12, Q13, Q14, Q15, Q16, Q17]), "operationType" : NewBodyOperationType.ADD, "endBound" : BoundingType.SYMMETRIC, "depth" : 10 * mm});
        }
    });
